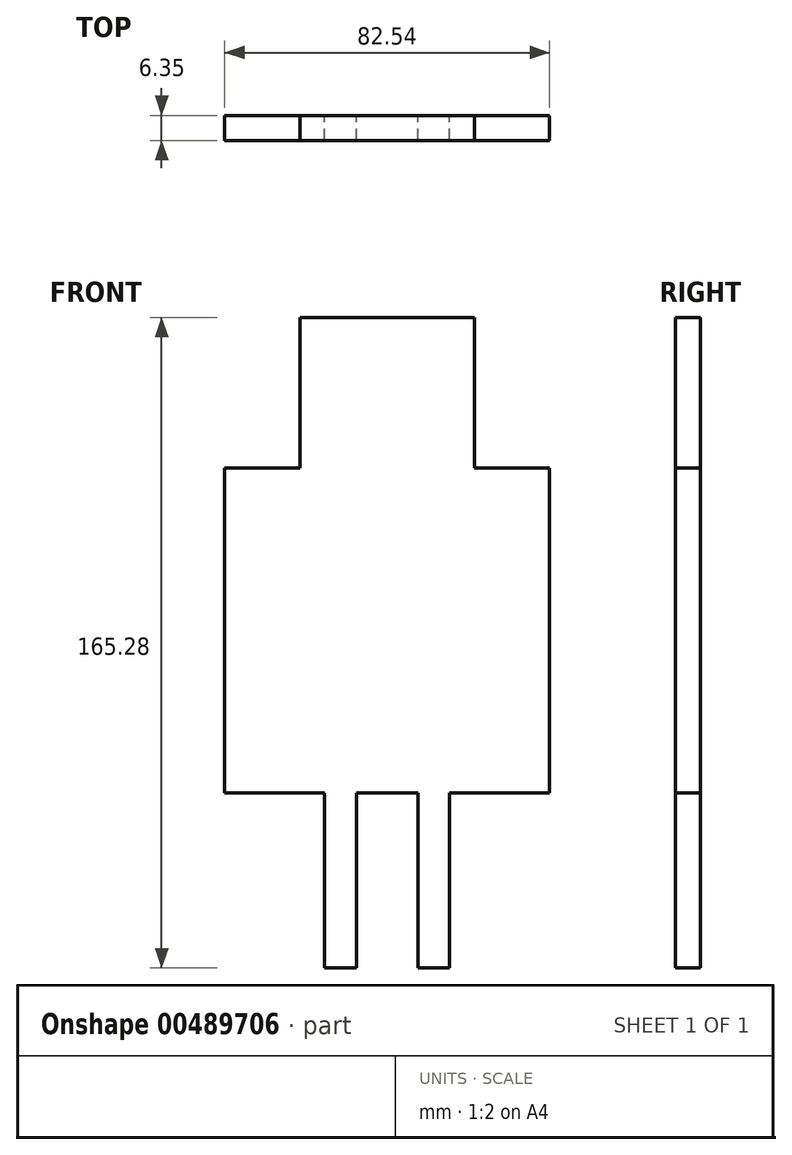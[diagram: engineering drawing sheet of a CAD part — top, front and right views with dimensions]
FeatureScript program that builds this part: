
annotation { "Feature Type Name" : "Feature", "Feature Type Description" : "" }
export const myFeature = defineFeature(function(context is Context, id is Id, definition is map)
    precondition{}
    {
        {
            var Q0;
            Q0=qCreatedBy(makeId("Front.planeOp"),FACE);
            var sketch = newSketch(context, id + "F0", { "sketchPlane" : qUnion([Q0])});
            skLineSegment(sketch, "E0.bottom", {"start": v(41.28, 41.28) * mm, "end": v(-41.27, 41.28) * mm});
            skLineSegment(sketch, "E0.top", {"start": v(41.28, -41.28) * mm, "end": v(7.82, -41.28) * mm});
            skLineSegment(sketch, "E0.left", {"start": v(41.28, 41.28) * mm, "end": v(41.28, -41.28) * mm});
            skLineSegment(sketch, "E0.right", {"start": v(-41.28, 41.28) * mm, "end": v(-41.28, -41.28) * mm});
            skPoint(sketch, "E0.middle", {"position": v(0, 0) * mm});
            skLineSegment(sketch, "E1.bottom", {"start": v(-41.27, 41.28) * mm, "end": v(41.28, 41.28) * mm});
            skLineSegment(sketch, "E1.top", {"start": v(-22.13, 79.56) * mm, "end": v(22.13, 79.56) * mm});
            skLineSegment(sketch, "E2.top", {"start": v(-41.27, 41.28) * mm, "end": v(-22.13, 41.28) * mm});
            skLineSegment(sketch, "E2.right", {"start": v(-22.13, 79.56) * mm, "end": v(-22.13, 41.28) * mm});
            skLineSegment(sketch, "E3.top", {"start": v(41.27, 41.28) * mm, "end": v(22.13, 41.28) * mm});
            skLineSegment(sketch, "E3.right", {"start": v(22.13, 79.56) * mm, "end": v(22.13, 41.28) * mm});
            skPoint(sketch, "E1.right.end.orphan", {"position": v(41.28, 79.56) * mm});
            skLineSegment(sketch, "E4.bottom", {"start": v(-41.27, -41.28) * mm, "end": v(-15.88, -41.28) * mm});
            skLineSegment(sketch, "E4.top", {"start": v(-15.88, -85.73) * mm, "end": v(-7.82, -85.73) * mm});
            skLineSegment(sketch, "E5.MirrorCS", {"start": v(-41.28, -41.27) * mm, "end": v(-15.88, -41.27) * mm});
            skLineSegment(sketch, "E6.MirrorCS", {"start": v(-15.88, -85.73) * mm, "end": v(-15.88, -41.27) * mm});
            skLineSegment(sketch, "E7.MirrorCS", {"start": v(15.88, -85.73) * mm, "end": v(15.88, -41.27) * mm});
            skPoint(sketch, "E8.top.end.orphan", {"position": v(-15.88, -130.18) * mm});
            skPoint(sketch, "E8.top.start.orphan", {"position": v(-41.28, -130.18) * mm});
            skPoint(sketch, "E9.MirrorCS.end.orphan", {"position": v(-41.28, -41.27) * mm});
            skPoint(sketch, "E8.bottom.end.orphan", {"position": v(-15.88, -85.73) * mm});
            skPoint(sketch, "E4.right.end.orphan", {"position": v(41.28, -85.73) * mm});
            skLineSegment(sketch, "E10.bottom", {"start": v(-7.82, -41.28) * mm, "end": v(-15.88, -41.28) * mm});
            skLineSegment(sketch, "E10.top", {"start": v(-7.82, -85.73) * mm, "end": v(-15.88, -85.73) * mm});
            skLineSegment(sketch, "E10.right", {"start": v(-15.88, -41.28) * mm, "end": v(-15.88, -85.73) * mm});
            skLineSegment(sketch, "E11.trimOffspring", {"start": v(7.82, -41.28) * mm, "end": v(41.28, -41.28) * mm});
            skLineSegment(sketch, "E12.trimOffspring", {"start": v(-7.82, -41.28) * mm, "end": v(-41.27, -41.28) * mm});
            skLineSegment(sketch, "E13.left", {"start": v(-7.82, -41.28) * mm, "end": v(-7.82, -85.6) * mm});
            skLineSegment(sketch, "E13.right", {"start": v(7.82, -41.28) * mm, "end": v(7.82, -85.6) * mm});
            skPoint(sketch, "E13.middle", {"position": v(0, -41.28) * mm});
            skLineSegment(sketch, "E14.left", {"start": v(-7.82, -85.6) * mm, "end": v(-7.82, -85.73) * mm});
            skLineSegment(sketch, "E14.right", {"start": v(7.82, -85.6) * mm, "end": v(7.82, -85.73) * mm});
            skPoint(sketch, "E13.bottom.end.orphan", {"position": v(7.82, 3.04) * mm});
            skPoint(sketch, "E13.bottom.start.orphan", {"position": v(-7.82, 3.04) * mm});
            skLineSegment(sketch, "E15.trimOffspring", {"start": v(7.82, -85.73) * mm, "end": v(15.88, -85.73) * mm});
            skLineSegment(sketch, "E16", {"start": v(-7.82, -41.28) * mm, "end": v(7.82, -41.28) * mm});
            skSolve(sketch);
        }
        {
            var Q0;
            Q0 = qSketchRegion(id + "F0", true);
            extrude(context, id + "F1", {"entities" : qUnion([Q0]), "depth" : 6.35 * mm});
        }
    });
